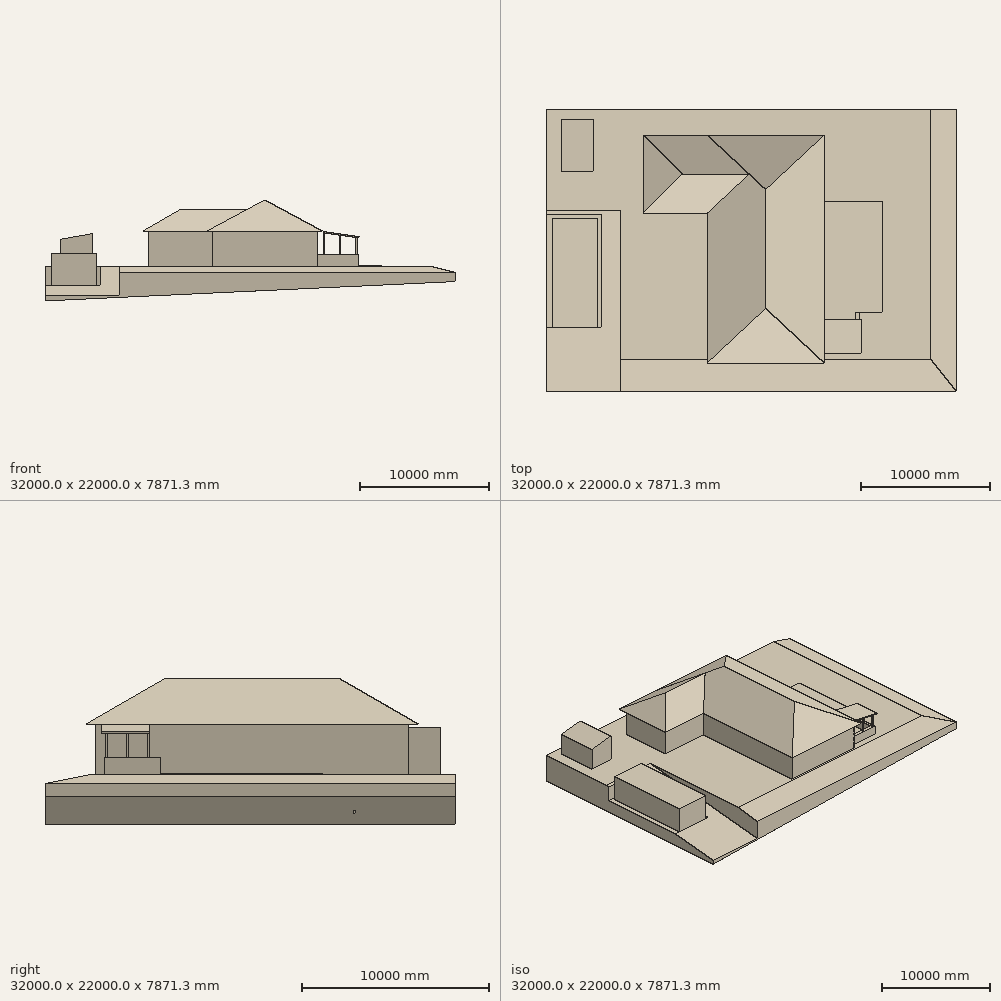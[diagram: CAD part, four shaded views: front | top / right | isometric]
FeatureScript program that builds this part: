
annotation { "Feature Type Name" : "Feature", "Feature Type Description" : "" }
export const myFeature = defineFeature(function(context is Context, id is Id, definition is map)
    precondition{}
    {
        {
            var Q0;
            Q0=qCreatedBy(makeId("Top.planeOp"),FACE);
            var sketch = newSketch(context, id + "F0", { "sketchPlane" : qUnion([Q0])});
            skLineSegment(sketch, "E0.bottom", {"start": v(0, 0) * mm, "end": v(32000, 0) * mm});
            skLineSegment(sketch, "E0.top", {"start": v(0, 22000) * mm, "end": v(32000, 22000) * mm});
            skLineSegment(sketch, "E0.left", {"start": v(0, 0) * mm, "end": v(0, 22000) * mm});
            skLineSegment(sketch, "E0.right", {"start": v(32000, 0) * mm, "end": v(32000, 22000) * mm});
            skLineSegment(sketch, "E1.bottom", {"start": v(13060, 2700) * mm, "end": v(21200, 2700) * mm});
            skLineSegment(sketch, "E1.top", {"start": v(13060, 19500) * mm, "end": v(21200, 19500) * mm});
            skLineSegment(sketch, "E1.left", {"start": v(13060, 2700) * mm, "end": v(13060, 19500) * mm});
            skLineSegment(sketch, "E1.right", {"start": v(21200, 2700) * mm, "end": v(21200, 19500) * mm});
            skLineSegment(sketch, "E2.bottom", {"start": v(13060, 19500) * mm, "end": v(8060, 19500) * mm});
            skLineSegment(sketch, "E2.top", {"start": v(13060, 14387.77) * mm, "end": v(8060, 14387.77) * mm});
            skLineSegment(sketch, "E2.left", {"start": v(13060, 19500) * mm, "end": v(13060, 14387.77) * mm});
            skLineSegment(sketch, "E2.right", {"start": v(8060, 19500) * mm, "end": v(8060, 14387.77) * mm});
            skLineSegment(sketch, "E3.bottom", {"start": v(1200, 21200) * mm, "end": v(3700, 21200) * mm});
            skLineSegment(sketch, "E3.top", {"start": v(1200, 17200) * mm, "end": v(3700, 17200) * mm});
            skLineSegment(sketch, "E3.left", {"start": v(1200, 21200) * mm, "end": v(1200, 17200) * mm});
            skLineSegment(sketch, "E3.right", {"start": v(3700, 21200) * mm, "end": v(3700, 17200) * mm});
            skLineSegment(sketch, "E4", {"start": v(21200, 3145.57) * mm, "end": v(24415.93, 3145.57) * mm});
            skLineSegment(sketch, "E5", {"start": v(24415.93, 3145.57) * mm, "end": v(24415.93, 6145.57) * mm});
            skLineSegment(sketch, "E6.0", {"start": v(24115.93, 3445.57) * mm, "end": v(24115.93, 6145.57) * mm});
            skLineSegment(sketch, "E6.1", {"start": v(21200, 3445.57) * mm, "end": v(24115.93, 3445.57) * mm});
            skLineSegment(sketch, "E7", {"start": v(24115.93, 6145.57) * mm, "end": v(24415.93, 6145.57) * mm});
            skLineSegment(sketch, "E8", {"start": v(21200, 3145.57) * mm, "end": v(21200, 3445.57) * mm});
            skLineSegment(sketch, "E9.bottom", {"start": v(21200, 14839.24) * mm, "end": v(26211.92, 14839.24) * mm});
            skLineSegment(sketch, "E9.top", {"start": v(21200, 6145.57) * mm, "end": v(26211.92, 6145.57) * mm});
            skLineSegment(sketch, "E9.left", {"start": v(21200, 14839.24) * mm, "end": v(21200, 6145.57) * mm});
            skLineSegment(sketch, "E9.right", {"start": v(26211.92, 14839.24) * mm, "end": v(26211.92, 6145.57) * mm});
            skLineSegment(sketch, "E10.bottom", {"start": v(0, 13800) * mm, "end": v(4300, 13800) * mm});
            skLineSegment(sketch, "E10.top", {"start": v(0, 5000) * mm, "end": v(4300, 5000) * mm});
            skLineSegment(sketch, "E10.left", {"start": v(0, 13800) * mm, "end": v(0, 5000) * mm});
            skLineSegment(sketch, "E10.right", {"start": v(4300, 13800) * mm, "end": v(4300, 5000) * mm});
            skLineSegment(sketch, "E11.bottom", {"start": v(0, 14800) * mm, "end": v(5800, 14800) * mm});
            skLineSegment(sketch, "E11.top", {"start": v(0, 0) * mm, "end": v(5800, 0) * mm});
            skLineSegment(sketch, "E11.left", {"start": v(0, 14800) * mm, "end": v(0, 0) * mm});
            skLineSegment(sketch, "E11.right", {"start": v(5800, 14800) * mm, "end": v(5800, 0) * mm});
            skLineSegment(sketch, "E12.left", {"start": v(13060, 19500) * mm, "end": v(13060, 17125.06) * mm});
            skLineSegment(sketch, "E13.bottom", {"start": v(20900, 19200) * mm, "end": v(17500, 19200) * mm});
            skLineSegment(sketch, "E13.top", {"start": v(20900, 17827) * mm, "end": v(17500, 17827) * mm});
            skLineSegment(sketch, "E13.left", {"start": v(21200, 19500) * mm, "end": v(21200, 17857.14) * mm});
            skLineSegment(sketch, "E13.right", {"start": v(17500, 19200) * mm, "end": v(17500, 17827) * mm});
            skLineSegment(sketch, "E14.left", {"start": v(21200, 17727) * mm, "end": v(21200, 14286) * mm});
            skLineSegment(sketch, "E15.left", {"start": v(13060, 19500) * mm, "end": v(13060, 16645) * mm});
            skLineSegment(sketch, "E15.right", {"start": v(16737, 19200) * mm, "end": v(16737, 16645) * mm});
            skLineSegment(sketch, "E16", {"start": v(17500, 17827) * mm, "end": v(16737, 17827) * mm});
            skLineSegment(sketch, "E17.0", {"start": v(16837, 19200) * mm, "end": v(16837, 16545) * mm});
            skLineSegment(sketch, "E17.1", {"start": v(13360, 16545) * mm, "end": v(16837, 16545) * mm});
            skLineSegment(sketch, "E18.0", {"start": v(17400, 19200) * mm, "end": v(17400, 17827) * mm});
            skLineSegment(sketch, "E19.0", {"start": v(20900, 14185) * mm, "end": v(18661.71, 14185) * mm});
            skLineSegment(sketch, "E20", {"start": v(20900, 6860) * mm, "end": v(13360, 6860) * mm});
            skLineSegment(sketch, "E21", {"start": v(13360, 6860) * mm, "end": v(13360, 14185) * mm});
            skLineSegment(sketch, "E22", {"start": v(13360, 14185) * mm, "end": v(18661.72, 14185) * mm});
            skLineSegment(sketch, "E23", {"start": v(16800, 14185) * mm, "end": v(16800, 10068) * mm});
            skLineSegment(sketch, "E24", {"start": v(16800, 10068) * mm, "end": v(13360, 10068) * mm});
            skLineSegment(sketch, "E25.0", {"start": v(16900, 9968) * mm, "end": v(13360, 9968) * mm});
            skLineSegment(sketch, "E25.1", {"start": v(16900, 14185) * mm, "end": v(16900, 9968) * mm});
            skLineSegment(sketch, "E26.0", {"start": v(20900, 6960) * mm, "end": v(13360, 6960) * mm});
            skLineSegment(sketch, "E27", {"start": v(17024, 6860) * mm, "end": v(17024, 3000) * mm});
            skLineSegment(sketch, "E28.0", {"start": v(17124, 6860) * mm, "end": v(17124, 3000) * mm});
            skLineSegment(sketch, "E29.0", {"start": v(17024, 5310) * mm, "end": v(13360, 5310) * mm});
            skLineSegment(sketch, "E30.0", {"start": v(13060, 14787.77) * mm, "end": v(8460, 14787.77) * mm});
            skLineSegment(sketch, "E30.1", {"start": v(8460, 19100) * mm, "end": v(8460, 14787.77) * mm});
            skLineSegment(sketch, "E30.2", {"start": v(13060, 19100) * mm, "end": v(8460, 19100) * mm});
            skLineSegment(sketch, "E31.0", {"start": v(13360, 19200) * mm, "end": v(20900, 19200) * mm});
            skLineSegment(sketch, "E32.0", {"start": v(20900, 3000) * mm, "end": v(20900, 19200) * mm});
            skLineSegment(sketch, "E33.0", {"start": v(13360, 3000) * mm, "end": v(13360, 19200) * mm});
            skLineSegment(sketch, "E34.0", {"start": v(13360, 3000) * mm, "end": v(20900, 3000) * mm});
            skLineSegment(sketch, "E35", {"start": v(16737, 16645) * mm, "end": v(13360, 16645) * mm});
            skLineSegment(sketch, "E36.0", {"start": v(20900, 14285) * mm, "end": v(18661.71, 14285) * mm});
            skLineSegment(sketch, "E36.1", {"start": v(13360, 14285) * mm, "end": v(18661.71, 14285) * mm});
            skLineSegment(sketch, "E37", {"start": v(18467, 17727) * mm, "end": v(18467, 14285) * mm});
            skLineSegment(sketch, "E38.0", {"start": v(18367, 17727) * mm, "end": v(18367, 14285) * mm});
            skLineSegment(sketch, "E39.0", {"start": v(17024, 5210) * mm, "end": v(13360, 5210) * mm});
            skLineSegment(sketch, "E40", {"start": v(13360, 16645) * mm, "end": v(10960, 16645) * mm});
            skLineSegment(sketch, "E41", {"start": v(10960, 16645) * mm, "end": v(10960, 14787.77) * mm});
            skLineSegment(sketch, "E42.0", {"start": v(11060, 16545) * mm, "end": v(11060, 14787.77) * mm});
            skLineSegment(sketch, "E42.1", {"start": v(13360, 16545) * mm, "end": v(11060, 16545) * mm});
            skLineSegment(sketch, "E43.bottom", {"start": v(13360, 16545) * mm, "end": v(13060, 16545) * mm});
            skLineSegment(sketch, "E43.top", {"start": v(13360, 14787.77) * mm, "end": v(13060, 14787.77) * mm});
            skLineSegment(sketch, "E43.left", {"start": v(13360, 16545) * mm, "end": v(13360, 14787.77) * mm});
            skLineSegment(sketch, "E43.right", {"start": v(13060, 16545) * mm, "end": v(13060, 14787.77) * mm});
            skLineSegment(sketch, "E44", {"start": v(16837, 17727) * mm, "end": v(20900, 17727) * mm});
            skSolve(sketch);
        }
        {
            var Q0;
            {var subQ13=sQuery(id+"F0.wireOp",EDGE,"E1.bottom");Q0=makeQuery(id+"F0.imprint","IMPRINT",FACE,{"disambiguationData":[TD([[makeQuery(id+"F0.imprint","IMPRINT",EDGE,{"derivedFrom":subQ13}),1.0]])]});}
            var Q1;
            {var subQ6=sQuery(id+"F0.wireOp",EDGE,"E2.bottom");Q1=makeQuery(id+"F0.imprint","IMPRINT",FACE,{"disambiguationData":[TD([[makeQuery(id+"F0.imprint","IMPRINT",EDGE,{"derivedFrom":subQ6}),1.0]])]});}
            extrude(context, id + "F1", {"entities" : qUnion([Q0, Q1]), "depth" : 2700 * mm, "offsetDistance" : 25 * mm});
        }
        {
            var Q0;
            Q0=makeQuery(id+"F1.opExtrude","SWEPT_FACE",FACE,{"disambiguationData":[OSD([sQuery(id+"F0.wireOp",EDGE,"E1.bottom")])]});
            cPlane(context, id + "F2", {"entities" : qUnion([Q0]), "cplaneType" : CPlaneType.OFFSET, "offset" : 500 * mm, "width" : 150 * mm, "height" : 150 * mm});
        }
        {
            var Q0;
            Q0=makeQuery(id+"F1.opExtrude","SWEPT_FACE",FACE,{"disambiguationData":[OSD([sQuery(id+"F0.wireOp",EDGE,"E2.right")])]});
            cPlane(context, id + "F3", {"entities" : qUnion([Q0]), "cplaneType" : CPlaneType.OFFSET, "offset" : 500 * mm, "width" : 150 * mm, "height" : 150 * mm});
        }
        {
            var Q0;
            Q0=qCreatedBy(id+"F2.planeOp",FACE);
            var sketch = newSketch(context, id + "F4", { "sketchPlane" : qUnion([Q0])});
            skLineSegment(sketch, "E45", {"start": v(12560, 2700) * mm, "end": v(17130, 5162.24) * mm});
            skLineSegment(sketch, "E46", {"start": v(17130, 5162.24) * mm, "end": v(21700, 2700) * mm});
            skLineSegment(sketch, "E47", {"start": v(21700, 2700) * mm, "end": v(12560, 2700) * mm});
            skSolve(sketch);
        }
        {
            var Q0;
            Q0=qCreatedBy(id+"F3.planeOp",FACE);
            var sketch = newSketch(context, id + "F5", { "sketchPlane" : qUnion([Q0])});
            skLineSegment(sketch, "E48", {"start": v(-20000, 2700) * mm, "end": v(-13887.77, 2700) * mm});
            skLineSegment(sketch, "E49", {"start": v(-13887.77, 2700) * mm, "end": v(-16943.88, 4464.45) * mm});
            skLineSegment(sketch, "E50", {"start": v(-16943.88, 4464.45) * mm, "end": v(-20000, 2700) * mm});
            skSolve(sketch);
        }
        {
            var Q0;
            Q0=makeQuery(id+"F4.imprint","IMPRINT",FACE,{"disambiguationData":[TD([[makeQuery(id+"F4.imprint","IMPRINT",EDGE,{"derivedFrom":sQuery(id+"F4.wireOp",EDGE,"E45")}),-1.0]])]});
            extrude(context, id + "F6", {"entities" : qUnion([Q0]), "oppositeDirection" : true, "depth" : 18000 * mm, "offsetDistance" : 25 * mm});
        }
        {
            var Q0;
            Q0 = qSketchRegion(id + "F5", true);
            var Q1;
            Q1=makeQuery(id+"F6.opExtrude","SWEPT_FACE",FACE,{"disambiguationData":[OSD([sQuery(id+"F4.wireOp",EDGE,"E45")])]});
            extrude(context, id + "F7", {"entities" : qUnion([Q0]), "endBound" : BoundingType.UP_TO_SURFACE, "oppositeDirection" : true, "depth" : 25 * mm, "endBoundEntityFace" : qUnion([Q1]), "offsetDistance" : 25 * mm});
        }
        {
            var Q0;
            Q0=makeQuery(id+"F6.opExtrude","CAP_FACE",FACE,{"disambiguationData":[OSD([sQuery(id+"F4.wireOp",EDGE,"E45"),sQuery(id+"F4.wireOp",EDGE,"E46"),sQuery(id+"F4.wireOp",EDGE,"E47")])],"isStart":false});
            var Q1;
            Q1=makeQuery(id+"F7.opExtrude","SWEPT_FACE",FACE,{"disambiguationData":[OSD([sQuery(id+"F5.wireOp",EDGE,"E50")])]});
            extrude(context, id + "F8", {"entities" : qUnion([Q0]), "operationType" : NewBodyOperationType.REMOVE, "endBound" : BoundingType.UP_TO_SURFACE, "oppositeDirection" : true, "depth" : 25 * mm, "endBoundEntityFace" : qUnion([Q1]), "offsetDistance" : 25 * mm});
        }
        {
            var Q0;
            Q0=makeQuery(id+"F6.opExtrude","CAP_EDGE",EDGE,{"disambiguationData":[OSD([sQuery(id+"F4.wireOp",EDGE,"E47")])],"isStart":true});
            cPlane(context, id + "F9", {"entities" : qUnion([Q0]), "cplaneType" : CPlaneType.LINE_ANGLE, "offset" : 25 * mm, "angle" : 60 * degree, "width" : 150 * mm, "height" : 150 * mm});
        }
        {
            var Q0;
            Q0=makeQuery(id+"F6.opExtrude","CAP_FACE",FACE,{"disambiguationData":[OSD([sQuery(id+"F4.wireOp",EDGE,"E45"),sQuery(id+"F4.wireOp",EDGE,"E46"),sQuery(id+"F4.wireOp",EDGE,"E47")])],"isStart":true});
            var Q1;
            Q1=qCreatedBy(id+"F9.planeOp",FACE);
            extrude(context, id + "F10", {"entities" : qUnion([Q0]), "operationType" : NewBodyOperationType.REMOVE, "endBound" : BoundingType.UP_TO_SURFACE, "oppositeDirection" : true, "depth" : 25 * mm, "endBoundEntityFace" : qUnion([Q1]), "offsetDistance" : 25 * mm});
        }
        {
            var Q0;
            Q0=makeQuery(id+"F7.opExtrude","CAP_EDGE",EDGE,{"disambiguationData":[OSD([sQuery(id+"F5.wireOp",EDGE,"E48")])],"isStart":true});
            cPlane(context, id + "F11", {"entities" : qUnion([Q0]), "cplaneType" : CPlaneType.LINE_ANGLE, "offset" : 25 * mm, "angle" : 30 * degree, "width" : 150 * mm, "height" : 150 * mm});
        }
        {
            var Q0;
            Q0=makeQuery(id+"F7.opExtrude","CAP_FACE",FACE,{"disambiguationData":[OSD([sQuery(id+"F5.wireOp",EDGE,"E48"),sQuery(id+"F5.wireOp",EDGE,"E49"),sQuery(id+"F5.wireOp",EDGE,"E50")])],"isStart":true});
            var Q1;
            Q1=qCreatedBy(id+"F11.planeOp",FACE);
            extrude(context, id + "F12", {"entities" : qUnion([Q0]), "operationType" : NewBodyOperationType.REMOVE, "endBound" : BoundingType.UP_TO_SURFACE, "oppositeDirection" : true, "depth" : 25 * mm, "endBoundEntityFace" : qUnion([Q1]), "offsetDistance" : 25 * mm});
        }
        {
            var Q0;
            {var subQ9=sQuery(id+"F0.wireOp",EDGE,"E0.top");Q0=makeQuery(id+"F0.imprint","IMPRINT",FACE,{"disambiguationData":[TD([[makeQuery(id+"F0.imprint","IMPRINT",EDGE,{"derivedFrom":subQ9}),-1.0]])]});}
            cPlane(context, id + "F13", {"entities" : qUnion([Q0]), "cplaneType" : CPlaneType.OFFSET, "offset" : 1500 * mm, "oppositeDirection" : true, "width" : 150 * mm, "height" : 150 * mm});
        }
        {
            var Q0;
            Q0=qCreatedBy(id+"F13.planeOp",FACE);
            var sketch = newSketch(context, id + "F14", { "sketchPlane" : qUnion([Q0])});
            skLineSegment(sketch, "E51.bottom", {"start": v(500, 13500.27) * mm, "end": v(4000, 13500.27) * mm});
            skLineSegment(sketch, "E51.top", {"start": v(500, 5000.27) * mm, "end": v(4000, 5000.27) * mm});
            skLineSegment(sketch, "E51.left", {"start": v(500, 13500.27) * mm, "end": v(500, 5000.27) * mm});
            skLineSegment(sketch, "E51.right", {"start": v(4000, 13500.27) * mm, "end": v(4000, 5000.27) * mm});
            skSolve(sketch);
        }
        {
            var Q0;
            Q0=sQuery(id+"F0.wireOp",EDGE,"E3.left");
            cPlane(context, id + "F15", {"entities" : qUnion([Q0]), "cplaneType" : CPlaneType.LINE_ANGLE, "offset" : 25 * mm, "angle" : 90 * degree, "width" : 150 * mm, "height" : 150 * mm});
        }
        {
            var Q0;
            Q0=qCreatedBy(id+"F15.planeOp",FACE);
            var sketch = newSketch(context, id + "F16", { "sketchPlane" : qUnion([Q0])});
            skLineSegment(sketch, "E52", {"start": v(21478.31, 2100) * mm, "end": v(17096.64, 2100) * mm});
            skSolve(sketch);
        }
        {
            var Q0;
            Q0=sQuery(id+"F16.wireOp",EDGE,"E52");
            cPlane(context, id + "F17", {"entities" : qUnion([Q0]), "cplaneType" : CPlaneType.LINE_ANGLE, "offset" : 25 * mm, "angle" : 10 * degree, "width" : 150 * mm, "height" : 150 * mm});
        }
        {
            var Q0;
            Q0=makeQuery(id+"F0.imprint","IMPRINT",FACE,{"disambiguationData":[TD([[makeQuery(id+"F0.imprint","IMPRINT",EDGE,{"derivedFrom":sQuery(id+"F0.wireOp",EDGE,"E3.bottom")}),-1.0]])]});
            var Q1;
            Q1=qCreatedBy(id+"F17.planeOp",FACE);
            extrude(context, id + "F18", {"entities" : qUnion([Q0]), "endBound" : BoundingType.UP_TO_SURFACE, "depth" : 25 * mm, "endBoundEntityFace" : qUnion([Q1]), "offsetDistance" : 25 * mm});
        }
        {
            var Q0;
            {var subQ0=sQuery(id+"F0.wireOp",EDGE,"E4");Q0=makeQuery(id+"F0.imprint","IMPRINT",FACE,{"disambiguationData":[TD([[makeQuery(id+"F0.imprint","IMPRINT",EDGE,{"derivedFrom":subQ0}),1.0]])]});}
            extrude(context, id + "F19", {"entities" : qUnion([Q0]), "operationType" : NewBodyOperationType.ADD, "depth" : 900 * mm, "offsetDistance" : 25 * mm});
        }
        {
            var Q0;
            Q0=makeQuery(id+"F6.opExtrude","SWEPT_EDGE",EDGE,{"disambiguationData":[OSD([sQuery(id+"F4.wireOp",EDGE,"E46"),sQuery(id+"F4.wireOp",EDGE,"E47")])]});
            cPlane(context, id + "F20", {"entities" : qUnion([Q0]), "cplaneType" : CPlaneType.LINE_ANGLE, "offset" : 25 * mm, "angle" : 8 * degree, "oppositeDirection" : true, "width" : 150 * mm, "height" : 150 * mm});
        }
        {
            var Q0;
            Q0=qCreatedBy(id+"F20.planeOp",FACE);
            var sketch = newSketch(context, id + "F21", { "sketchPlane" : qUnion([Q0])});
            skLineSegment(sketch, "E53.bottom", {"start": v(21113.05, -5591.84) * mm, "end": v(23989.32, -5591.84) * mm});
            skLineSegment(sketch, "E53.top", {"start": v(21113.05, -2990.74) * mm, "end": v(23989.32, -2990.74) * mm});
            skLineSegment(sketch, "E53.left", {"start": v(21113.05, -5591.84) * mm, "end": v(21113.05, -2990.74) * mm});
            skLineSegment(sketch, "E53.right", {"start": v(23989.32, -5591.84) * mm, "end": v(23989.32, -2990.74) * mm});
            skSolve(sketch);
        }
        {
            var Q0;
            Q0=makeQuery(id+"F21.imprint","IMPRINT",FACE,{"disambiguationData":[TD([[makeQuery(id+"F21.imprint","IMPRINT",EDGE,{"derivedFrom":sQuery(id+"F21.wireOp",EDGE,"E53.bottom")}),1.0]])]});
            extrude(context, id + "F22", {"entities" : qUnion([Q0]), "depth" : 100 * mm, "offsetDistance" : 25 * mm});
        }
        {
            var Q0;
            Q0=makeQuery(id+"F19.opExtrude","CAP_FACE",FACE,{"disambiguationData":[OSD([sQuery(id+"F0.wireOp",EDGE,"E1.right"),sQuery(id+"F0.wireOp",EDGE,"E4"),sQuery(id+"F0.wireOp",EDGE,"E5"),sQuery(id+"F0.wireOp",EDGE,"E6.0"),sQuery(id+"F0.wireOp",EDGE,"E6.1"),sQuery(id+"F0.wireOp",EDGE,"E7")])],"isStart":false});
            var sketch = newSketch(context, id + "F23", { "sketchPlane" : qUnion([Q0])});
            skLineSegment(sketch, "E54.bottom", {"start": v(21700, 3345.57) * mm, "end": v(21800, 3345.57) * mm});
            skLineSegment(sketch, "E54.top", {"start": v(21700, 3245.57) * mm, "end": v(21800, 3245.57) * mm});
            skLineSegment(sketch, "E54.left", {"start": v(21700, 3345.57) * mm, "end": v(21700, 3245.57) * mm});
            skLineSegment(sketch, "E54.right", {"start": v(21800, 3345.57) * mm, "end": v(21800, 3245.57) * mm});
            skLineSegment(sketch, "E55.bottom", {"start": v(22958, 3345.57) * mm, "end": v(23058, 3345.57) * mm});
            skLineSegment(sketch, "E55.top", {"start": v(22958, 3245.57) * mm, "end": v(23058, 3245.57) * mm});
            skLineSegment(sketch, "E55.left", {"start": v(22958, 3345.57) * mm, "end": v(22958, 3245.57) * mm});
            skLineSegment(sketch, "E55.right", {"start": v(23058, 3345.57) * mm, "end": v(23058, 3245.57) * mm});
            skLineSegment(sketch, "E56.bottom", {"start": v(24215.93, 3345.57) * mm, "end": v(24315.93, 3345.57) * mm});
            skLineSegment(sketch, "E56.top", {"start": v(24215.93, 3245.57) * mm, "end": v(24315.93, 3245.57) * mm});
            skLineSegment(sketch, "E56.left", {"start": v(24215.93, 3345.57) * mm, "end": v(24215.93, 3245.57) * mm});
            skLineSegment(sketch, "E56.right", {"start": v(24315.93, 3345.57) * mm, "end": v(24315.93, 3245.57) * mm});
            skLineSegment(sketch, "E57.bottom", {"start": v(24215.93, 4468.84) * mm, "end": v(24315.93, 4468.84) * mm});
            skLineSegment(sketch, "E57.top", {"start": v(24215.93, 4368.84) * mm, "end": v(24315.93, 4368.84) * mm});
            skLineSegment(sketch, "E57.left", {"start": v(24215.93, 4468.84) * mm, "end": v(24215.93, 4368.84) * mm});
            skLineSegment(sketch, "E57.right", {"start": v(24315.93, 4468.84) * mm, "end": v(24315.93, 4368.84) * mm});
            skLineSegment(sketch, "E58.bottom", {"start": v(24215.93, 5591.84) * mm, "end": v(24315.93, 5591.84) * mm});
            skLineSegment(sketch, "E58.top", {"start": v(24215.93, 5491.84) * mm, "end": v(24315.93, 5491.84) * mm});
            skLineSegment(sketch, "E58.left", {"start": v(24215.93, 5591.84) * mm, "end": v(24215.93, 5491.84) * mm});
            skLineSegment(sketch, "E58.right", {"start": v(24315.93, 5591.84) * mm, "end": v(24315.93, 5491.84) * mm});
            skSolve(sketch);
        }
        {
            var Q0;
            Q0 = qSketchRegion(id + "F23", true);
            var Q1;
            Q1=makeQuery(id+"F22.opExtrude","CAP_FACE",FACE,{"disambiguationData":[OSD([sQuery(id+"F21.wireOp",EDGE,"E53.bottom"),sQuery(id+"F21.wireOp",EDGE,"E53.top"),sQuery(id+"F21.wireOp",EDGE,"E53.left"),sQuery(id+"F21.wireOp",EDGE,"E53.right")])],"isStart":false});
            extrude(context, id + "F24", {"entities" : qUnion([Q0]), "endBound" : BoundingType.UP_TO_SURFACE, "depth" : 25 * mm, "endBoundEntityFace" : qUnion([Q1]), "offsetDistance" : 25 * mm});
        }
        {
            var Q0;
            Q0=sQuery(id+"F0.wireOp",EDGE,"E0.right");
            cPlane(context, id + "F25", {"entities" : qUnion([Q0]), "cplaneType" : CPlaneType.LINE_ANGLE, "offset" : 25 * mm, "angle" : 90 * degree, "width" : 150 * mm, "height" : 150 * mm});
        }
        {
            var Q0;
            Q0=qCreatedBy(id+"F25.planeOp",FACE);
            var sketch = newSketch(context, id + "F26", { "sketchPlane" : qUnion([Q0])});
            skLineSegment(sketch, "E59", {"start": v(5918.85, -1200) * mm, "end": v(13232.15, -1200) * mm});
            skSolve(sketch);
        }
        {
            var Q0;
            Q0=sQuery(id+"F26.wireOp",EDGE,"E59");
            cPlane(context, id + "F27", {"entities" : qUnion([Q0]), "cplaneType" : CPlaneType.LINE_ANGLE, "offset" : 25 * mm, "angle" : 2.7 * degree, "oppositeDirection" : true, "width" : 150 * mm, "height" : 150 * mm});
        }
        {
            var Q0;
            {var subQ0=sQuery(id+"F0.wireOp",EDGE,"E7");Q0=makeQuery(id+"F0.imprint","IMPRINT",FACE,{"disambiguationData":[TD([[makeQuery(id+"F0.imprint","IMPRINT",EDGE,{"derivedFrom":subQ0}),1.0]])]});}
            var Q1;
            {var subQ4=sQuery(id+"F0.wireOp",EDGE,"E6.0");Q1=makeQuery(id+"F0.imprint","IMPRINT",FACE,{"disambiguationData":[TD([[makeQuery(id+"F0.imprint","IMPRINT",EDGE,{"derivedFrom":subQ4}),1.0]])]});}
            extrude(context, id + "F28", {"entities" : qUnion([Q0, Q1]), "operationType" : NewBodyOperationType.ADD, "depth" : 25 * mm, "offsetDistance" : 25 * mm});
        }
        {
            var Q0;
            {var subQ2=sQuery(id+"F0.wireOp",EDGE,"E10.bottom");Q0=makeQuery(id+"F0.imprint","IMPRINT",FACE,{"disambiguationData":[TD([[makeQuery(id+"F0.imprint","IMPRINT",EDGE,{"derivedFrom":subQ2}),-1.0]])]});}
            var Q1;
            Q1=qCreatedBy(id+"F13.planeOp",FACE);
            extrude(context, id + "F29", {"entities" : qUnion([Q0]), "operationType" : NewBodyOperationType.REMOVE, "endBound" : BoundingType.UP_TO_SURFACE, "oppositeDirection" : true, "depth" : 25 * mm, "endBoundEntityFace" : qUnion([Q1]), "offsetDistance" : 25 * mm});
        }
        {
            var Q0;
            Q0=sQuery(id+"F0.wireOp",EDGE,"E11.left");
            cPlane(context, id + "F30", {"entities" : qUnion([Q0]), "cplaneType" : CPlaneType.LINE_ANGLE, "offset" : 500 * mm, "angle" : 90 * degree, "width" : 150 * mm, "height" : 150 * mm});
        }
        {
            var Q0;
            Q0=qCreatedBy(id+"F30.planeOp",FACE);
            var sketch = newSketch(context, id + "F31", { "sketchPlane" : qUnion([Q0])});
            skLineSegment(sketch, "E60", {"start": v(14138.71, 0) * mm, "end": v(5000.27, -1500) * mm});
            skSolve(sketch);
        }
        {
            var Q0;
            Q0=sQuery(id+"F31.wireOp",EDGE,"E60");
            cPlane(context, id + "F32", {"entities" : qUnion([Q0]), "cplaneType" : CPlaneType.LINE_ANGLE, "offset" : 25 * mm, "angle" : 0 * degree, "width" : 150 * mm, "height" : 150 * mm});
        }
        {
            var Q0;
            Q0=makeQuery(id+"F0.imprint","IMPRINT",FACE,{"disambiguationData":[TD([[makeQuery(id+"F0.imprint","IMPRINT",EDGE,{"derivedFrom":sQuery(id+"F0.wireOp",EDGE,"E3.bottom")}),-1.0]])]});
            var Q1;
            {var subQ9=sQuery(id+"F0.wireOp",EDGE,"E0.top");Q1=makeQuery(id+"F0.imprint","IMPRINT",FACE,{"disambiguationData":[TD([[makeQuery(id+"F0.imprint","IMPRINT",EDGE,{"derivedFrom":subQ9}),-1.0]])]});}
            var Q2;
            {var subQ6=sQuery(id+"F0.wireOp",EDGE,"E2.bottom");Q2=makeQuery(id+"F0.imprint","IMPRINT",FACE,{"disambiguationData":[TD([[makeQuery(id+"F0.imprint","IMPRINT",EDGE,{"derivedFrom":subQ6}),1.0]])]});}
            var Q3;
            {var subQ13=sQuery(id+"F0.wireOp",EDGE,"E1.bottom");Q3=makeQuery(id+"F0.imprint","IMPRINT",FACE,{"disambiguationData":[TD([[makeQuery(id+"F0.imprint","IMPRINT",EDGE,{"derivedFrom":subQ13}),1.0]])]});}
            var Q4;
            {var subQ0=sQuery(id+"F0.wireOp",EDGE,"E7");Q4=makeQuery(id+"F0.imprint","IMPRINT",FACE,{"disambiguationData":[TD([[makeQuery(id+"F0.imprint","IMPRINT",EDGE,{"derivedFrom":subQ0}),1.0]])]});}
            var Q5;
            {var subQ4=sQuery(id+"F0.wireOp",EDGE,"E6.0");Q5=makeQuery(id+"F0.imprint","IMPRINT",FACE,{"disambiguationData":[TD([[makeQuery(id+"F0.imprint","IMPRINT",EDGE,{"derivedFrom":subQ4}),1.0]])]});}
            var Q6;
            {var subQ0=sQuery(id+"F0.wireOp",EDGE,"E4");Q6=makeQuery(id+"F0.imprint","IMPRINT",FACE,{"disambiguationData":[TD([[makeQuery(id+"F0.imprint","IMPRINT",EDGE,{"derivedFrom":subQ0}),1.0]])]});}
            var Q7;
            {var subQ4=sQuery(id+"F0.wireOp",EDGE,"E10.bottom");Q7=makeQuery(id+"F0.imprint","IMPRINT",FACE,{"disambiguationData":[TD([[makeQuery(id+"F0.imprint","IMPRINT",EDGE,{"derivedFrom":subQ4}),1.0]])]});}
            var Q8;
            {var subQ2=sQuery(id+"F0.wireOp",EDGE,"E10.bottom");Q8=makeQuery(id+"F0.imprint","IMPRINT",FACE,{"disambiguationData":[TD([[makeQuery(id+"F0.imprint","IMPRINT",EDGE,{"derivedFrom":subQ2}),-1.0]])]});}
            var Q9;
            Q9=qCreatedBy(id+"F27.planeOp",FACE);
            extrude(context, id + "F33", {"entities" : qUnion([Q0, Q1, Q2, Q3, Q4, Q5, Q6, Q7, Q8]), "endBound" : BoundingType.UP_TO_SURFACE, "oppositeDirection" : true, "depth" : 25 * mm, "endBoundEntityFace" : qUnion([Q9]), "offsetDistance" : 25 * mm});
        }
        {
            var Q0;
            {var subQ2=sQuery(id+"F0.wireOp",EDGE,"E10.bottom");Q0=makeQuery(id+"F0.imprint","IMPRINT",FACE,{"disambiguationData":[TD([[makeQuery(id+"F0.imprint","IMPRINT",EDGE,{"derivedFrom":subQ2}),-1.0]])]});}
            var Q1;
            {var subQ4=sQuery(id+"F0.wireOp",EDGE,"E10.bottom");Q1=makeQuery(id+"F0.imprint","IMPRINT",FACE,{"disambiguationData":[TD([[makeQuery(id+"F0.imprint","IMPRINT",EDGE,{"derivedFrom":subQ4}),1.0]])]});}
            var Q2;
            Q2=qCreatedBy(id+"F32.planeOp",FACE);
            extrude(context, id + "F34", {"entities" : qUnion([Q0, Q1]), "operationType" : NewBodyOperationType.REMOVE, "endBound" : BoundingType.UP_TO_SURFACE, "oppositeDirection" : true, "depth" : 25 * mm, "endBoundEntityFace" : qUnion([Q2]), "offsetDistance" : 25 * mm});
        }
        {
            var Q0;
            {var subQ2=sQuery(id+"F0.wireOp",EDGE,"E10.bottom");Q0=makeQuery(id+"F0.imprint","IMPRINT",FACE,{"disambiguationData":[TD([[makeQuery(id+"F0.imprint","IMPRINT",EDGE,{"derivedFrom":subQ2}),-1.0]])]});}
            var Q1;
            Q1=qCreatedBy(id+"F13.planeOp",FACE);
            extrude(context, id + "F35", {"entities" : qUnion([Q0]), "operationType" : NewBodyOperationType.REMOVE, "endBound" : BoundingType.UP_TO_SURFACE, "oppositeDirection" : true, "depth" : 25 * mm, "endBoundEntityFace" : qUnion([Q1]), "offsetDistance" : 25 * mm});
        }
        {
            var Q0;
            Q0=makeQuery(id+"F33.opExtrude","CAP_EDGE",EDGE,{"disambiguationData":[OSD([sQuery(id+"F0.wireOp",EDGE,"E0.bottom")])],"isStart":true});
            chamfer(context, id + "F36", {"entities" : qUnion([Q0]), "chamferType" : ChamferType.TWO_OFFSETS, "width1" : 2500 * mm, "oppositeDirection" : false, "width2" : 500 * mm, "tangentPropagation" : true});
        }
        {
            var Q0;
            Q0=makeQuery(id+"F14.imprint","IMPRINT",FACE,{"disambiguationData":[TD([[makeQuery(id+"F14.imprint","IMPRINT",EDGE,{"derivedFrom":sQuery(id+"F14.wireOp",EDGE,"E51.bottom")}),-1.0]])]});
            extrude(context, id + "F37", {"entities" : qUnion([Q0]), "operationType" : NewBodyOperationType.ADD, "depth" : 2500 * mm, "offsetDistance" : 25 * mm});
        }
        {
            var Q0;
            Q0=makeQuery(id+"F33.opExtrude","CAP_EDGE",EDGE,{"disambiguationData":[OSD([sQuery(id+"F0.wireOp",EDGE,"E0.right")])],"isStart":true});
            chamfer(context, id + "F38", {"entities" : qUnion([Q0]), "chamferType" : ChamferType.TWO_OFFSETS, "width1" : 2000 * mm, "oppositeDirection" : false, "width2" : 500 * mm, "tangentPropagation" : true});
        }
        {
            var Q0;
            {var subQ2=sQuery(id+"F0.wireOp",EDGE,"E25.0");Q0=makeQuery(id+"F0.imprint","IMPRINT",FACE,{"disambiguationData":[TD([[makeQuery(id+"F0.imprint","IMPRINT",EDGE,{"derivedFrom":subQ2}),1.0]])]});}
            var Q1;
            {var subQ3=sQuery(id+"F0.wireOp",EDGE,"E28.0");Q1=makeQuery(id+"F0.imprint","IMPRINT",FACE,{"disambiguationData":[TD([[makeQuery(id+"F0.imprint","IMPRINT",EDGE,{"derivedFrom":subQ3}),1.0]])]});}
            var Q2;
            {var subQ5=sQuery(id+"F0.wireOp",EDGE,"E29.0");Q2=makeQuery(id+"F0.imprint","IMPRINT",FACE,{"disambiguationData":[TD([[makeQuery(id+"F0.imprint","IMPRINT",EDGE,{"derivedFrom":subQ5}),-1.0]])]});}
            var Q3;
            {var subQ0=sQuery(id+"F0.wireOp",EDGE,"E39.0");Q3=makeQuery(id+"F0.imprint","IMPRINT",FACE,{"disambiguationData":[TD([[makeQuery(id+"F0.imprint","IMPRINT",EDGE,{"derivedFrom":subQ0}),1.0]])]});}
            var Q4;
            {var subQ7=sQuery(id+"F0.wireOp",EDGE,"E28.0");Q4=makeQuery(id+"F0.imprint","IMPRINT",FACE,{"disambiguationData":[TD([[makeQuery(id+"F0.imprint","IMPRINT",EDGE,{"derivedFrom":subQ7}),-1.0]])]});}
            var Q5;
            {var subQ2=sQuery(id+"F0.wireOp",EDGE,"E29.0");Q5=makeQuery(id+"F0.imprint","IMPRINT",FACE,{"disambiguationData":[TD([[makeQuery(id+"F0.imprint","IMPRINT",EDGE,{"derivedFrom":subQ2}),1.0]])]});}
            var Q6;
            {var subQ5=sQuery(id+"F0.wireOp",EDGE,"E26.0");Q6=makeQuery(id+"F0.imprint","IMPRINT",FACE,{"disambiguationData":[TD([[makeQuery(id+"F0.imprint","IMPRINT",EDGE,{"derivedFrom":subQ5}),1.0]])]});}
            var Q7;
            {var subQ4=sQuery(id+"F0.wireOp",EDGE,"E23");Q7=makeQuery(id+"F0.imprint","IMPRINT",FACE,{"disambiguationData":[TD([[makeQuery(id+"F0.imprint","IMPRINT",EDGE,{"derivedFrom":subQ4}),-1.0]])]});}
            var Q8;
            {var subQ3=sQuery(id+"F0.wireOp",EDGE,"E23");Q8=makeQuery(id+"F0.imprint","IMPRINT",FACE,{"disambiguationData":[TD([[makeQuery(id+"F0.imprint","IMPRINT",EDGE,{"derivedFrom":subQ3}),1.0]])]});}
            var Q9;
            {var subQ4=sQuery(id+"F0.wireOp",EDGE,"E17.1");Q9=makeQuery(id+"F0.imprint","IMPRINT",FACE,{"disambiguationData":[TD([[makeQuery(id+"F0.imprint","IMPRINT",EDGE,{"derivedFrom":subQ4}),-1.0]])]});}
            var Q10;
            {var subQ1=sQuery(id+"F0.wireOp",EDGE,"E36.0");Q10=makeQuery(id+"F0.imprint","IMPRINT",FACE,{"disambiguationData":[TD([[makeQuery(id+"F0.imprint","IMPRINT",EDGE,{"derivedFrom":subQ1}),1.0]])]});}
            var Q11;
            {var subQ2=sQuery(id+"F0.wireOp",EDGE,"E36.0");Q11=makeQuery(id+"F0.imprint","IMPRINT",FACE,{"disambiguationData":[TD([[makeQuery(id+"F0.imprint","IMPRINT",EDGE,{"derivedFrom":subQ2}),-1.0]])]});}
            var Q12;
            {var subQ0=sQuery(id+"F0.wireOp",EDGE,"E37");Q12=makeQuery(id+"F0.imprint","IMPRINT",FACE,{"disambiguationData":[TD([[makeQuery(id+"F0.imprint","IMPRINT",EDGE,{"derivedFrom":subQ0}),-1.0]])]});}
            var Q13;
            {var subQ0=sQuery(id+"F0.wireOp",EDGE,"E13.bottom");Q13=makeQuery(id+"F0.imprint","IMPRINT",FACE,{"disambiguationData":[TD([[makeQuery(id+"F0.imprint","IMPRINT",EDGE,{"derivedFrom":subQ0}),1.0]])]});}
            var Q14;
            {var subQ0=sQuery(id+"F0.wireOp",EDGE,"E18.0");Q14=makeQuery(id+"F0.imprint","IMPRINT",FACE,{"disambiguationData":[TD([[makeQuery(id+"F0.imprint","IMPRINT",EDGE,{"derivedFrom":subQ0}),-1.0]])]});}
            var Q15;
            {var subQ3=sQuery(id+"F0.wireOp",EDGE,"E35");Q15=makeQuery(id+"F0.imprint","IMPRINT",FACE,{"disambiguationData":[TD([[makeQuery(id+"F0.imprint","IMPRINT",EDGE,{"derivedFrom":subQ3}),-1.0]])]});}
            var Q16;
            {var subQ1=sQuery(id+"F0.wireOp",EDGE,"E13.top");Q16=makeQuery(id+"F0.imprint","IMPRINT",FACE,{"disambiguationData":[TD([[makeQuery(id+"F0.imprint","IMPRINT",EDGE,{"derivedFrom":subQ1}),1.0]])]});}
            var Q17;
            {var subQ0=sQuery(id+"F0.wireOp",EDGE,"E13.right");Q17=makeQuery(id+"F0.imprint","IMPRINT",FACE,{"disambiguationData":[TD([[makeQuery(id+"F0.imprint","IMPRINT",EDGE,{"derivedFrom":subQ0}),-1.0]])]});}
            var Q18;
            {var subQ0=sQuery(id+"F0.wireOp",EDGE,"E31.0");var subQ1=sQuery(id+"F0.wireOp",EDGE,"E15.right");var subQ2=makeQuery(id+"F0.imprint","INTERSECT",VERTEX,{"derivedFrom":[subQ1,subQ0]});Q18=makeQuery(id+"F0.imprint","IMPRINT",FACE,{"disambiguationData":[TD([[makeQuery(id+"F0.imprint","IMPRINT",EDGE,{"disambiguationData":[TD([[subQ2,-1.0]])],"derivedFrom":subQ1}),1.0]])]});}
            var Q19;
            {var subQ5=sQuery(id+"F0.wireOp",EDGE,"E42.0");Q19=makeQuery(id+"F0.imprint","IMPRINT",FACE,{"disambiguationData":[TD([[makeQuery(id+"F0.imprint","IMPRINT",EDGE,{"derivedFrom":subQ5}),1.0]])]});}
            var Q20;
            Q20=qCreatedBy(id+"F27.planeOp",FACE);
            extrude(context, id + "F39", {"entities" : qUnion([Q0, Q1, Q2, Q3, Q4, Q5, Q6, Q7, Q8, Q9, Q10, Q11, Q12, Q13, Q14, Q15, Q16, Q17, Q18, Q19]), "operationType" : NewBodyOperationType.ADD, "endBound" : BoundingType.UP_TO_SURFACE, "oppositeDirection" : true, "depth" : 25 * mm, "endBoundEntityFace" : qUnion([Q20]), "offsetDistance" : 25 * mm});
        }
        {
            var Q0;
            {var subQ2=sQuery(id+"F0.wireOp",EDGE,"E29.0");Q0=makeQuery(id+"F0.imprint","IMPRINT",FACE,{"disambiguationData":[TD([[makeQuery(id+"F0.imprint","IMPRINT",EDGE,{"derivedFrom":subQ2}),1.0]])]});}
            var Q1;
            {var subQ7=sQuery(id+"F0.wireOp",EDGE,"E28.0");Q1=makeQuery(id+"F0.imprint","IMPRINT",FACE,{"disambiguationData":[TD([[makeQuery(id+"F0.imprint","IMPRINT",EDGE,{"derivedFrom":subQ7}),-1.0]])]});}
            var Q2;
            {var subQ5=sQuery(id+"F0.wireOp",EDGE,"E26.0");Q2=makeQuery(id+"F0.imprint","IMPRINT",FACE,{"disambiguationData":[TD([[makeQuery(id+"F0.imprint","IMPRINT",EDGE,{"derivedFrom":subQ5}),1.0]])]});}
            var Q3;
            {var subQ3=sQuery(id+"F0.wireOp",EDGE,"E23");Q3=makeQuery(id+"F0.imprint","IMPRINT",FACE,{"disambiguationData":[TD([[makeQuery(id+"F0.imprint","IMPRINT",EDGE,{"derivedFrom":subQ3}),1.0]])]});}
            var Q4;
            {var subQ1=sQuery(id+"F0.wireOp",EDGE,"E36.0");Q4=makeQuery(id+"F0.imprint","IMPRINT",FACE,{"disambiguationData":[TD([[makeQuery(id+"F0.imprint","IMPRINT",EDGE,{"derivedFrom":subQ1}),1.0]])]});}
            var Q5;
            {var subQ0=sQuery(id+"F0.wireOp",EDGE,"E37");Q5=makeQuery(id+"F0.imprint","IMPRINT",FACE,{"disambiguationData":[TD([[makeQuery(id+"F0.imprint","IMPRINT",EDGE,{"derivedFrom":subQ0}),-1.0]])]});}
            var Q6;
            {var subQ0=sQuery(id+"F0.wireOp",EDGE,"E31.0");var subQ1=sQuery(id+"F0.wireOp",EDGE,"E15.right");var subQ2=makeQuery(id+"F0.imprint","INTERSECT",VERTEX,{"derivedFrom":[subQ1,subQ0]});Q6=makeQuery(id+"F0.imprint","IMPRINT",FACE,{"disambiguationData":[TD([[makeQuery(id+"F0.imprint","IMPRINT",EDGE,{"disambiguationData":[TD([[subQ2,-1.0]])],"derivedFrom":subQ1}),1.0]])]});}
            var Q7;
            {var subQ1=sQuery(id+"F0.wireOp",EDGE,"E13.top");Q7=makeQuery(id+"F0.imprint","IMPRINT",FACE,{"disambiguationData":[TD([[makeQuery(id+"F0.imprint","IMPRINT",EDGE,{"derivedFrom":subQ1}),1.0]])]});}
            var Q8;
            {var subQ0=sQuery(id+"F0.wireOp",EDGE,"E13.right");Q8=makeQuery(id+"F0.imprint","IMPRINT",FACE,{"disambiguationData":[TD([[makeQuery(id+"F0.imprint","IMPRINT",EDGE,{"derivedFrom":subQ0}),-1.0]])]});}
            extrude(context, id + "F40", {"entities" : qUnion([Q0, Q1, Q2, Q3, Q4, Q5, Q6, Q7, Q8]), "depth" : 2700 * mm, "offsetDistance" : 25 * mm});
        }
        {
            var Q0;
            {var subQ0=sQuery(id+"F0.wireOp",EDGE,"E30.1");Q0=makeQuery(id+"F0.imprint","IMPRINT",FACE,{"disambiguationData":[TD([[makeQuery(id+"F0.imprint","IMPRINT",EDGE,{"derivedFrom":subQ0}),1.0]])]});}
            var Q1;
            {var subQ3=sQuery(id+"F0.wireOp",EDGE,"E43.top");Q1=makeQuery(id+"F0.imprint","IMPRINT",FACE,{"disambiguationData":[TD([[makeQuery(id+"F0.imprint","IMPRINT",EDGE,{"derivedFrom":subQ3}),-1.0]])]});}
            var Q2;
            {var subQ0=sQuery(id+"F0.wireOp",EDGE,"E40");var subQ1=sQuery(id+"F0.wireOp",EDGE,"E1.left");var subQ2=makeQuery(id+"F0.imprint","INTERSECT",VERTEX,{"derivedFrom":[subQ1,subQ0]});Q2=makeQuery(id+"F0.imprint","IMPRINT",FACE,{"disambiguationData":[TD([[makeQuery(id+"F0.imprint","IMPRINT",EDGE,{"disambiguationData":[TD([[subQ2,1.0]])],"derivedFrom":subQ1}),-1.0]])]});}
            var Q3;
            {var subQ0=sQuery(id+"F0.wireOp",EDGE,"E41");Q3=makeQuery(id+"F0.imprint","IMPRINT",FACE,{"disambiguationData":[TD([[makeQuery(id+"F0.imprint","IMPRINT",EDGE,{"derivedFrom":subQ0}),1.0]])]});}
            var Q4;
            Q4=qCreatedBy(id+"F27.planeOp",FACE);
            extrude(context, id + "F41", {"entities" : qUnion([Q0, Q1, Q2, Q3]), "operationType" : NewBodyOperationType.ADD, "endBound" : BoundingType.UP_TO_SURFACE, "oppositeDirection" : true, "depth" : 25 * mm, "endBoundEntityFace" : qUnion([Q4]), "offsetDistance" : 25 * mm});
        }
        {
            var Q0;
            {var subQ0=sQuery(id+"F0.wireOp",EDGE,"E40");var subQ1=sQuery(id+"F0.wireOp",EDGE,"E1.left");var subQ2=makeQuery(id+"F0.imprint","INTERSECT",VERTEX,{"derivedFrom":[subQ1,subQ0]});Q0=makeQuery(id+"F0.imprint","IMPRINT",FACE,{"disambiguationData":[TD([[makeQuery(id+"F0.imprint","IMPRINT",EDGE,{"disambiguationData":[TD([[subQ2,1.0]])],"derivedFrom":subQ1}),-1.0]])]});}
            var Q1;
            {var subQ0=sQuery(id+"F0.wireOp",EDGE,"E41");Q1=makeQuery(id+"F0.imprint","IMPRINT",FACE,{"disambiguationData":[TD([[makeQuery(id+"F0.imprint","IMPRINT",EDGE,{"derivedFrom":subQ0}),1.0]])]});}
            extrude(context, id + "F42", {"entities" : qUnion([Q0, Q1]), "depth" : 2700 * mm, "offsetDistance" : 25 * mm});
        }
    });
